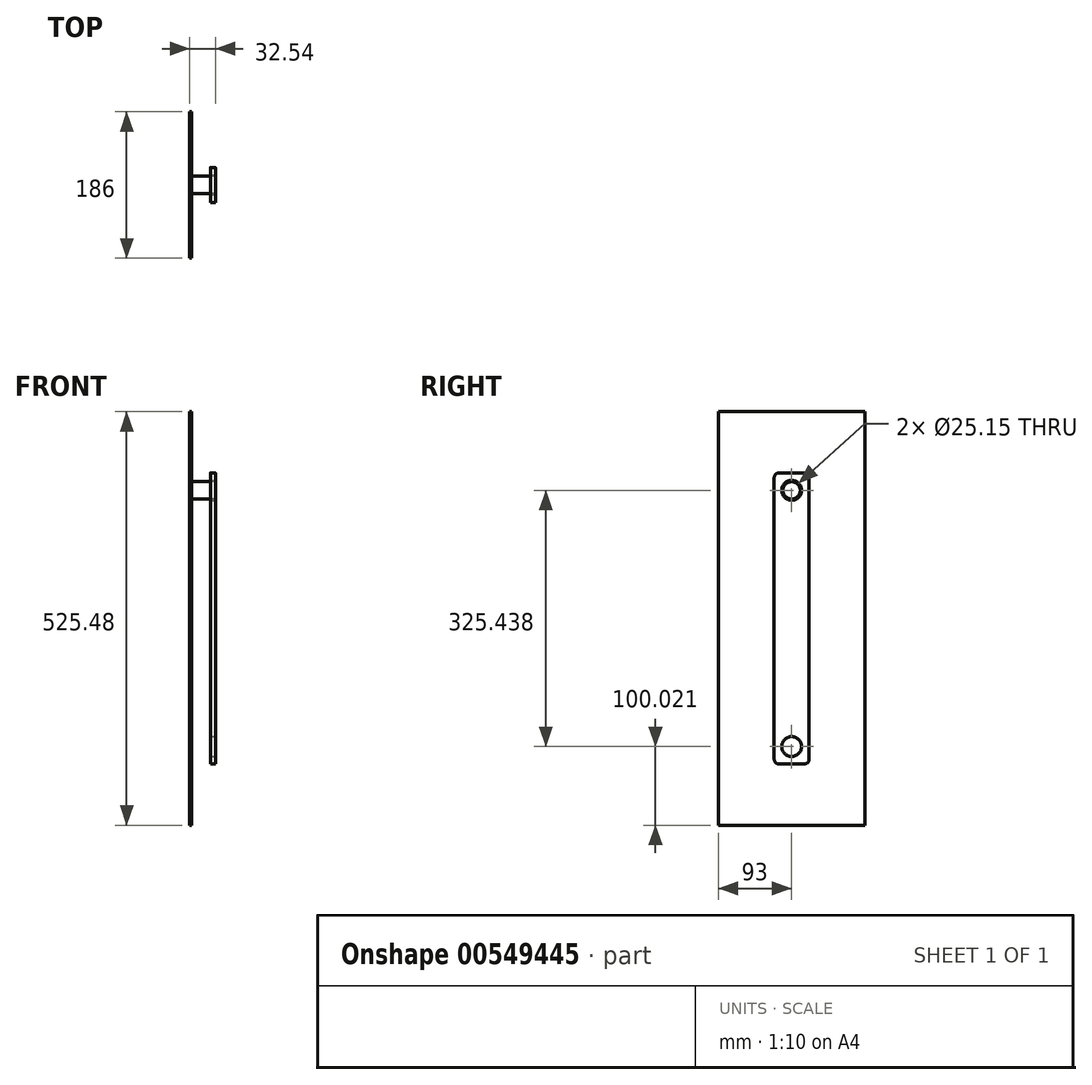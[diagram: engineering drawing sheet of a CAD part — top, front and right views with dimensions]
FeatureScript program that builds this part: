
annotation { "Feature Type Name" : "Feature", "Feature Type Description" : "" }
export const myFeature = defineFeature(function(context is Context, id is Id, definition is map)
    precondition{}
    {
        {
            var Q0;
            Q0=qCreatedBy(makeId("Right.planeOp"),FACE);
            var sketch = newSketch(context, id + "F0", { "sketchPlane" : qUnion([Q0])});
            skCircle(sketch, "E0", {"center": v(0, 162.72) * mm, "radius": 10.99 * mm});
            skCircle(sketch, "E1.MirrorC", {"center": v(0, -162.72) * mm, "radius": 10.99 * mm});
            skSolve(sketch);
        }
        {
            var Q0;
            Q0=makeQuery(id+"F0.imprint","IMPRINT",FACE,{"disambiguationData":[TD([[makeQuery(id+"F0.imprint","IMPRINT",EDGE,{"derivedFrom":sQuery(id+"F0.wireOp",EDGE,"E1.MirrorC")}),-1.0]])]});
            var Q1;
            Q1=makeQuery(id+"F0.imprint","IMPRINT",FACE,{"disambiguationData":[TD([[makeQuery(id+"F0.imprint","IMPRINT",EDGE,{"derivedFrom":sQuery(id+"F0.wireOp",EDGE,"E0")}),1.0]])]});
            extrude(context, id + "F1", {"entities" : qUnion([Q0, Q1]), "depth" : 30 * mm, "offsetDistance" : 25.4 * mm});
        }
        {
            var Q0;
            Q0=makeQuery(id+"F1.opExtrude","CAP_FACE",FACE,{"disambiguationData":[OSD([sQuery(id+"F0.wireOp",EDGE,"E0")])],"isStart":true});
            var sketch = newSketch(context, id + "F2", { "sketchPlane" : qUnion([Q0])});
            skPoint(sketch, "E2.0", {"position": v(0, 0) * mm});
            skLineSegment(sketch, "E3.bottom", {"start": v(-93, 262.74) * mm, "end": v(93, 262.74) * mm});
            skLineSegment(sketch, "E3.top", {"start": v(-93, -262.74) * mm, "end": v(93, -262.74) * mm});
            skLineSegment(sketch, "E3.left", {"start": v(-93, 262.74) * mm, "end": v(-93, -262.74) * mm});
            skLineSegment(sketch, "E3.right", {"start": v(93, 262.74) * mm, "end": v(93, -262.74) * mm});
            skSolve(sketch);
        }
        {
            var Q0;
            Q0 = qSketchRegion(id + "F2", true);
            extrude(context, id + "F3", {"entities" : qUnion([Q0]), "depth" : 2.54 * mm, "offsetDistance" : 25.4 * mm});
        }
        {
            var Q0;
            Q0=makeQuery(id+"F1.opExtrude","CAP_FACE",FACE,{"disambiguationData":[OSD([sQuery(id+"F0.wireOp",EDGE,"E0")])],"isStart":false});
            var sketch = newSketch(context, id + "F4", { "sketchPlane" : qUnion([Q0])});
            skCircle(sketch, "E4.0", {"center": v(0, 162.72) * mm, "radius": 10.99 * mm});
            skPoint(sketch, "E5.0", {"position": v(0, 0) * mm});
            skLineSegment(sketch, "E6.bottom", {"start": v(-22.23, 184.94) * mm, "end": v(22.23, 184.94) * mm});
            skLineSegment(sketch, "E6.top", {"start": v(-22.23, -184.94) * mm, "end": v(22.23, -184.94) * mm});
            skLineSegment(sketch, "E6.left", {"start": v(-22.23, 184.94) * mm, "end": v(-22.23, -184.94) * mm});
            skLineSegment(sketch, "E6.right", {"start": v(22.23, 184.94) * mm, "end": v(22.23, -184.94) * mm});
            skCircle(sketch, "E7.0", {"center": v(0, -162.72) * mm, "radius": 10.99 * mm});
            skCircle(sketch, "E8.0", {"center": v(0, -162.72) * mm, "radius": 12.57 * mm});
            skCircle(sketch, "E9.0", {"center": v(0, 162.72) * mm, "radius": 12.57 * mm});
            skSolve(sketch);
        }
        {
            var Q0;
            Q0=makeQuery(id+"F4.imprint","IMPRINT",FACE,{"disambiguationData":[TD([[makeQuery(id+"F4.imprint","IMPRINT",EDGE,{"derivedFrom":sQuery(id+"F4.wireOp",EDGE,"E6.bottom")}),-1.0]])]});
            extrude(context, id + "F5", {"entities" : qUnion([Q0]), "oppositeDirection" : true, "depth" : 6.35 * mm, "offsetDistance" : 25.4 * mm});
        }
        {
            var Q0;
            Q0=makeQuery(id+"F5.opExtrude","SWEPT_EDGE",EDGE,{"disambiguationData":[OSD([sQuery(id+"F4.wireOp",EDGE,"E6.bottom"),sQuery(id+"F4.wireOp",EDGE,"E6.left")])]});
            var Q1;
            Q1=makeQuery(id+"F5.opExtrude","SWEPT_EDGE",EDGE,{"disambiguationData":[OSD([sQuery(id+"F4.wireOp",EDGE,"E6.bottom"),sQuery(id+"F4.wireOp",EDGE,"E6.right")])]});
            var Q2;
            Q2=makeQuery(id+"F5.opExtrude","SWEPT_EDGE",EDGE,{"disambiguationData":[OSD([sQuery(id+"F4.wireOp",EDGE,"E6.top"),sQuery(id+"F4.wireOp",EDGE,"E6.right")])]});
            var Q3;
            Q3=makeQuery(id+"F5.opExtrude","SWEPT_EDGE",EDGE,{"disambiguationData":[OSD([sQuery(id+"F4.wireOp",EDGE,"E6.top"),sQuery(id+"F4.wireOp",EDGE,"E6.left")])]});
            fillet(context, id + "F6", {"entities" : qUnion([Q0, Q1, Q2, Q3]), "radius" : 6.35 * mm, "tangentPropagation" : true, "allowEdgeOverflow" : false});
        }
    });
